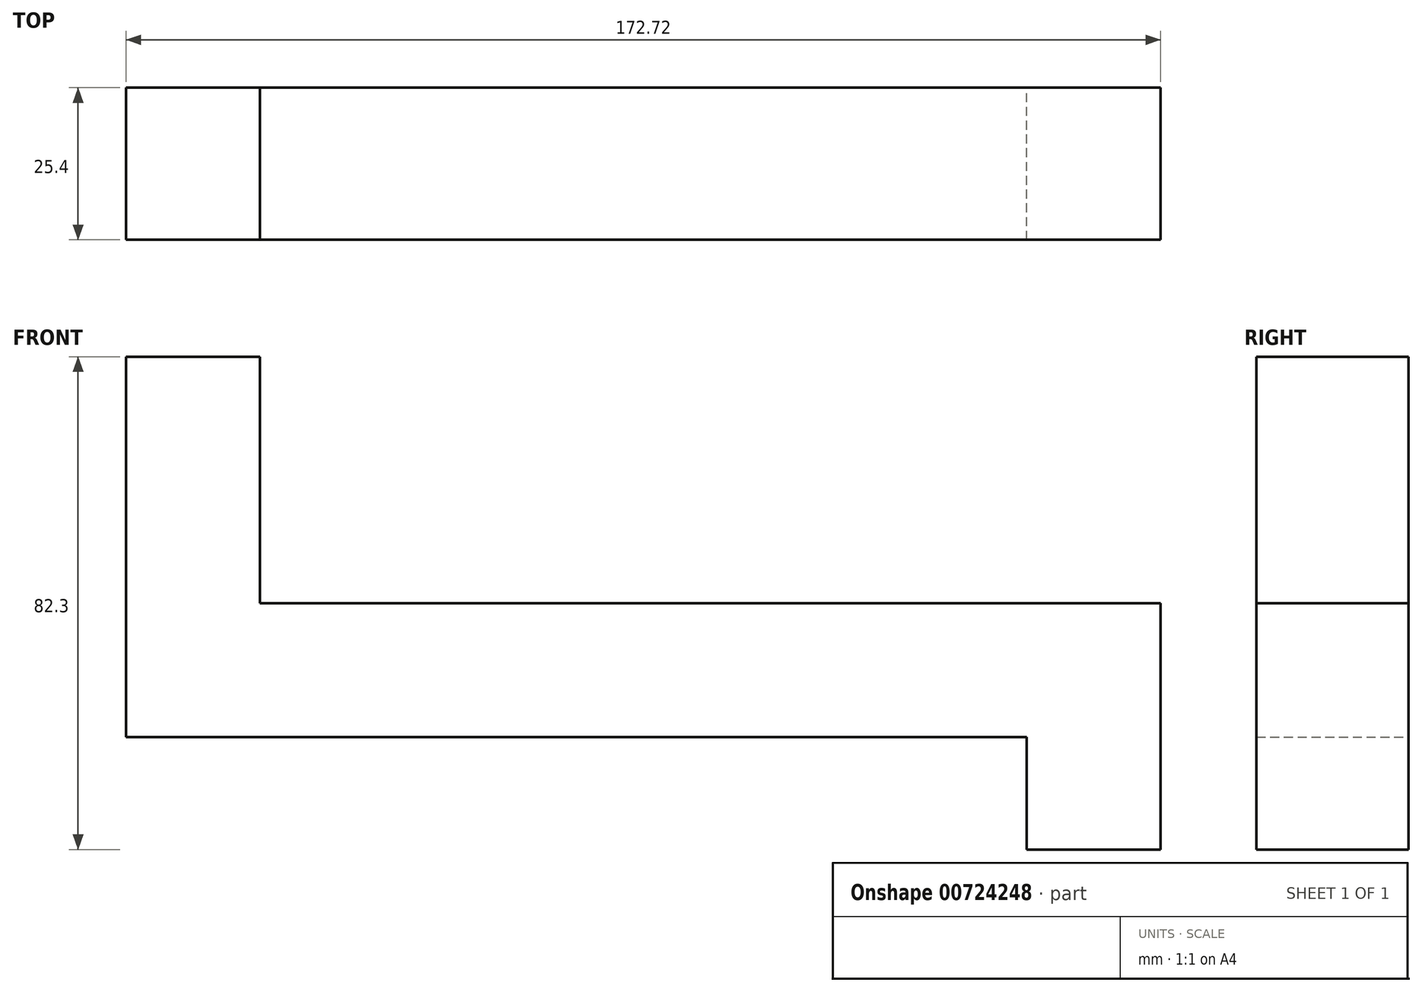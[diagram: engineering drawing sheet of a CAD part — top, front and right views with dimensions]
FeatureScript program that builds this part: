
annotation { "Feature Type Name" : "Feature", "Feature Type Description" : "" }
export const myFeature = defineFeature(function(context is Context, id is Id, definition is map)
    precondition{}
    {
        {
            var Q0;
            Q0=qCreatedBy(makeId("Front.planeOp"),FACE);
            var sketch = newSketch(context, id + "F0", { "sketchPlane" : qUnion([Q0])});
            skLineSegment(sketch, "E0", {"start": v(-60.82, 54.31) * mm, "end": v(-60.82, -9.19) * mm});
            skLineSegment(sketch, "E1", {"start": v(89.55, -9.19) * mm, "end": v(-60.82, -9.19) * mm});
            skLineSegment(sketch, "E2", {"start": v(89.55, -9.19) * mm, "end": v(89.55, -27.99) * mm});
            skLineSegment(sketch, "E3", {"start": v(111.9, -27.99) * mm, "end": v(89.55, -27.99) * mm});
            skLineSegment(sketch, "E4", {"start": v(-60.82, 54.31) * mm, "end": v(-38.47, 54.31) * mm});
            skLineSegment(sketch, "E5", {"start": v(111.9, -27.99) * mm, "end": v(111.9, 13.16) * mm});
            skLineSegment(sketch, "E6", {"start": v(-38.47, 54.31) * mm, "end": v(-38.47, 13.16) * mm});
            skLineSegment(sketch, "E7", {"start": v(-38.47, 13.16) * mm, "end": v(111.9, 13.16) * mm});
            skSolve(sketch);
        }
        {
            var Q0;
            Q0=makeQuery(id+"F0.imprint","IMPRINT",FACE,{"disambiguationData":[TD([[makeQuery(id+"F0.imprint","IMPRINT",EDGE,{"derivedFrom":sQuery(id+"F0.wireOp",EDGE,"E0")}),1.0]])]});
            extrude(context, id + "F1", {"entities" : qUnion([Q0]), "depth" : 25.4 * mm, "offsetDistance" : 25.4 * mm});
        }
    });
